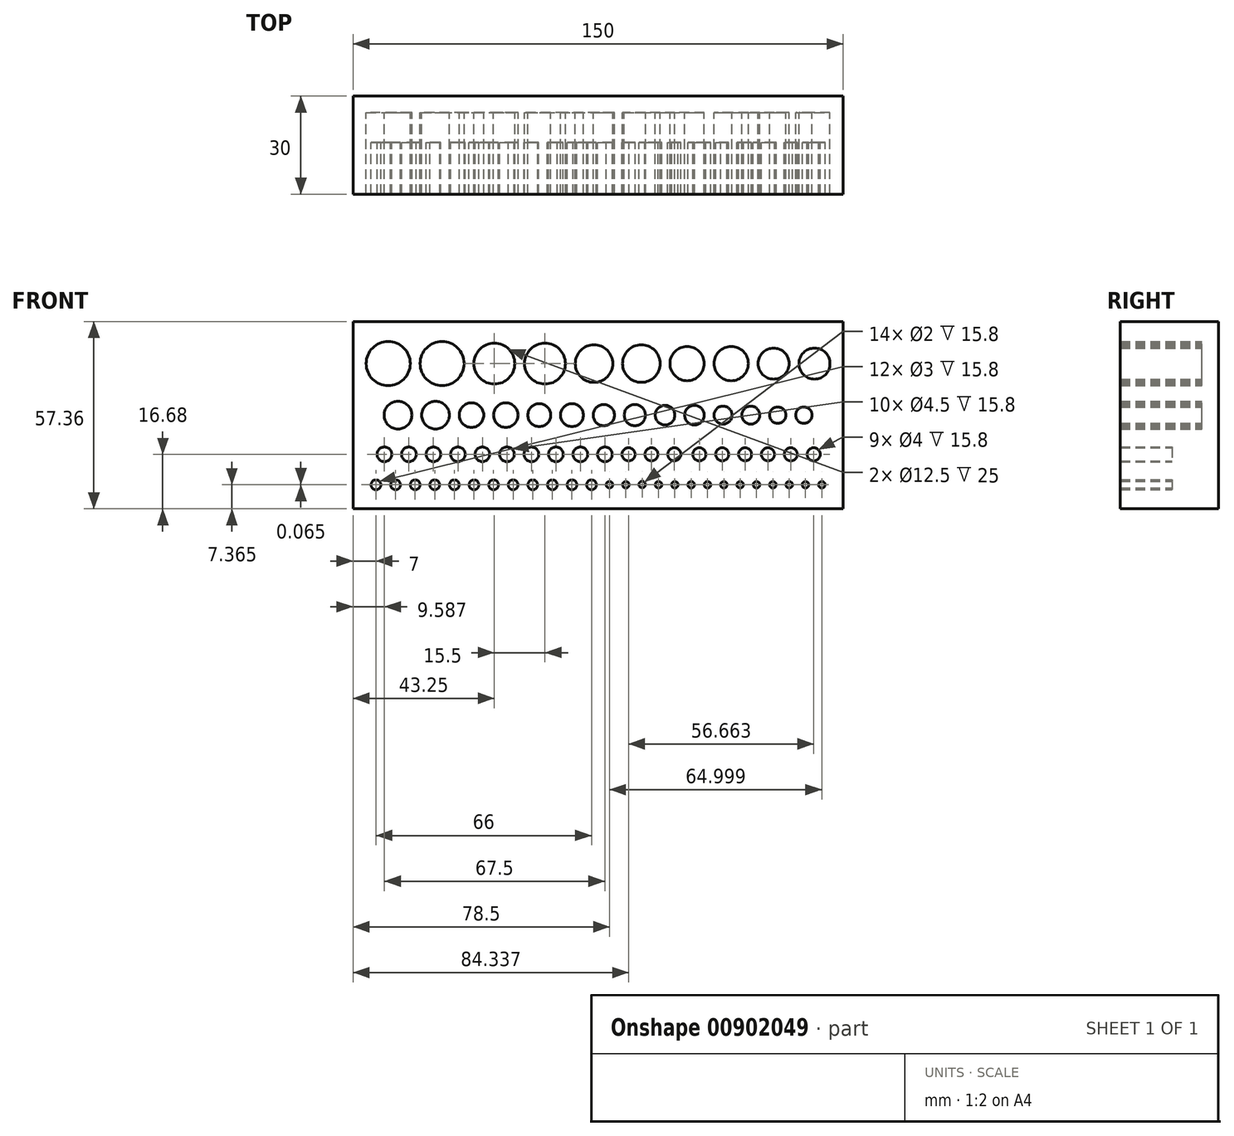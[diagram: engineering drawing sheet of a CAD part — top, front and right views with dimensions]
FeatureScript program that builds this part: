
annotation { "Feature Type Name" : "Feature", "Feature Type Description" : "" }
export const myFeature = defineFeature(function(context is Context, id is Id, definition is map)
    precondition{}
    {
        {
            var Q0;
            Q0=qCreatedBy(makeId("Front.planeOp"),FACE);
            var sketch = newSketch(context, id + "F0", { "sketchPlane" : qUnion([Q0])});
            skLineSegment(sketch, "E0.bottom", {"start": v(75, 28.68) * mm, "end": v(-75, 28.68) * mm});
            skLineSegment(sketch, "E0.top", {"start": v(75, -28.68) * mm, "end": v(-75, -28.68) * mm});
            skLineSegment(sketch, "E0.left", {"start": v(75, 28.68) * mm, "end": v(75, -28.68) * mm});
            skLineSegment(sketch, "E0.right", {"start": v(-75, 28.68) * mm, "end": v(-75, -28.68) * mm});
            skPoint(sketch, "E0.middle", {"position": v(0, 0) * mm});
            skLineSegment(sketch, "E1", {"start": v(-75, 0) * mm, "end": v(75, 0) * mm});
            skLineSegment(sketch, "E2", {"start": v(-75, 15.78) * mm, "end": v(75, 15.78) * mm});
            skLineSegment(sketch, "E3", {"start": v(-75, -12) * mm, "end": v(75, -12) * mm});
            skCircle(sketch, "E4", {"center": v(-64.25, 15.78) * mm, "radius": 6.75 * mm});
            skCircle(sketch, "E5", {"center": v(-47.75, 15.78) * mm, "radius": 6.75 * mm});
            skCircle(sketch, "E6", {"center": v(-31.75, 15.78) * mm, "radius": 6.25 * mm});
            skCircle(sketch, "E7", {"center": v(-16.25, 15.78) * mm, "radius": 6.25 * mm});
            skCircle(sketch, "E8", {"center": v(-1.25, 15.78) * mm, "radius": 5.75 * mm});
            skCircle(sketch, "E9", {"center": v(13.25, 15.78) * mm, "radius": 5.75 * mm});
            skCircle(sketch, "E10", {"center": v(27.25, 15.78) * mm, "radius": 5.25 * mm});
            skCircle(sketch, "E11", {"center": v(40.75, 15.78) * mm, "radius": 5.25 * mm});
            skCircle(sketch, "E12", {"center": v(53.75, 15.78) * mm, "radius": 4.75 * mm});
            skCircle(sketch, "E13", {"center": v(66.25, 15.78) * mm, "radius": 4.75 * mm});
            skCircle(sketch, "E14", {"center": v(-61.25, 0) * mm, "radius": 4.25 * mm});
            skCircle(sketch, "E15", {"center": v(-49.75, 0) * mm, "radius": 4.25 * mm});
            skCircle(sketch, "E16", {"center": v(-38.75, 0) * mm, "radius": 3.75 * mm});
            skCircle(sketch, "E17", {"center": v(-28.25, 0) * mm, "radius": 3.75 * mm});
            skCircle(sketch, "E18", {"center": v(-18, 0) * mm, "radius": 3.5 * mm});
            skCircle(sketch, "E19", {"center": v(-8, 0) * mm, "radius": 3.5 * mm});
            skCircle(sketch, "E20", {"center": v(1.75, 0) * mm, "radius": 3.25 * mm});
            skCircle(sketch, "E21", {"center": v(11.25, 0) * mm, "radius": 3.25 * mm});
            skCircle(sketch, "E22", {"center": v(20.5, 0) * mm, "radius": 3 * mm});
            skCircle(sketch, "E23", {"center": v(29.5, 0) * mm, "radius": 3 * mm});
            skCircle(sketch, "E24", {"center": v(38.25, 0) * mm, "radius": 2.75 * mm});
            skCircle(sketch, "E25", {"center": v(46.75, 0) * mm, "radius": 2.75 * mm});
            skCircle(sketch, "E26", {"center": v(55, 0) * mm, "radius": 2.5 * mm});
            skCircle(sketch, "E27", {"center": v(63, 0) * mm, "radius": 2.5 * mm});
            skCircle(sketch, "E28", {"center": v(-65.41, -12) * mm, "radius": 2.25 * mm});
            skCircle(sketch, "E29", {"center": v(-57.91, -12) * mm, "radius": 2.25 * mm});
            skCircle(sketch, "E30", {"center": v(-50.41, -12) * mm, "radius": 2.25 * mm});
            skCircle(sketch, "E31", {"center": v(-42.91, -12) * mm, "radius": 2.25 * mm});
            skCircle(sketch, "E32", {"center": v(-35.41, -12) * mm, "radius": 2.25 * mm});
            skCircle(sketch, "E33", {"center": v(-27.91, -12) * mm, "radius": 2.25 * mm});
            skCircle(sketch, "E34", {"center": v(-20.41, -12) * mm, "radius": 2.25 * mm});
            skCircle(sketch, "E35", {"center": v(-12.91, -12) * mm, "radius": 2.25 * mm});
            skCircle(sketch, "E36", {"center": v(-5.41, -12) * mm, "radius": 2.25 * mm});
            skCircle(sketch, "E37", {"center": v(2.09, -12) * mm, "radius": 2.25 * mm});
            skCircle(sketch, "E38", {"center": v(9.34, -12) * mm, "radius": 2 * mm});
            skCircle(sketch, "E39", {"center": v(16.34, -12) * mm, "radius": 2 * mm});
            skCircle(sketch, "E40", {"center": v(23.34, -12) * mm, "radius": 2 * mm});
            skCircle(sketch, "E41", {"center": v(31, -12) * mm, "radius": 2 * mm});
            skCircle(sketch, "E42", {"center": v(38, -12) * mm, "radius": 2 * mm});
            skCircle(sketch, "E43", {"center": v(45, -12) * mm, "radius": 2 * mm});
            skCircle(sketch, "E44", {"center": v(52, -12) * mm, "radius": 2 * mm});
            skCircle(sketch, "E45", {"center": v(59, -12) * mm, "radius": 2 * mm});
            skCircle(sketch, "E46", {"center": v(66, -12) * mm, "radius": 2 * mm});
            skLineSegment(sketch, "E47", {"start": v(-75, -21.32) * mm, "end": v(75, -21.32) * mm});
            skCircle(sketch, "E48", {"center": v(-68, -21.32) * mm, "radius": 1.5 * mm});
            skCircle(sketch, "E49", {"center": v(-62, -21.32) * mm, "radius": 1.5 * mm});
            skCircle(sketch, "E50", {"center": v(-56, -21.32) * mm, "radius": 1.5 * mm});
            skCircle(sketch, "E51", {"center": v(-50, -21.32) * mm, "radius": 1.5 * mm});
            skCircle(sketch, "E52", {"center": v(-44, -21.32) * mm, "radius": 1.5 * mm});
            skCircle(sketch, "E53", {"center": v(-38, -21.32) * mm, "radius": 1.5 * mm});
            skCircle(sketch, "E54", {"center": v(-32, -21.32) * mm, "radius": 1.5 * mm});
            skCircle(sketch, "E55", {"center": v(-26, -21.32) * mm, "radius": 1.5 * mm});
            skCircle(sketch, "E56", {"center": v(-20, -21.32) * mm, "radius": 1.5 * mm});
            skCircle(sketch, "E57", {"center": v(-14, -21.32) * mm, "radius": 1.5 * mm});
            skCircle(sketch, "E58", {"center": v(-8, -21.32) * mm, "radius": 1.5 * mm});
            skCircle(sketch, "E59", {"center": v(-2, -21.32) * mm, "radius": 1.5 * mm});
            skCircle(sketch, "E60", {"center": v(3.5, -21.32) * mm, "radius": 1 * mm});
            skCircle(sketch, "E61", {"center": v(8.5, -21.32) * mm, "radius": 1 * mm});
            skCircle(sketch, "E62", {"center": v(13.5, -21.25) * mm, "radius": 1 * mm});
            skCircle(sketch, "E63", {"center": v(18.5, -21.32) * mm, "radius": 1 * mm});
            skCircle(sketch, "E64", {"center": v(23.5, -21.32) * mm, "radius": 1 * mm});
            skCircle(sketch, "E65", {"center": v(28.5, -21.32) * mm, "radius": 1 * mm});
            skCircle(sketch, "E66", {"center": v(33.5, -21.32) * mm, "radius": 1 * mm});
            skCircle(sketch, "E67", {"center": v(38.5, -21.32) * mm, "radius": 1 * mm});
            skCircle(sketch, "E68", {"center": v(43.5, -21.32) * mm, "radius": 1 * mm});
            skCircle(sketch, "E69", {"center": v(48.5, -21.32) * mm, "radius": 1 * mm});
            skCircle(sketch, "E70", {"center": v(53.5, -21.32) * mm, "radius": 1 * mm});
            skCircle(sketch, "E71", {"center": v(58.5, -21.32) * mm, "radius": 1 * mm});
            skCircle(sketch, "E72", {"center": v(63.5, -21.32) * mm, "radius": 1 * mm});
            skCircle(sketch, "E73", {"center": v(68.5, -21.32) * mm, "radius": 1 * mm});
            skSolve(sketch);
        }
        {
            var Q0;
            Q0=qSketchRegion(id+"F0",true);
            extrude(context, id + "F1", {"entities" : qUnion([Q0]), "depth" : 25 * mm, "offsetDistance" : 25 * mm});
        }
        {
            var Q0;
            Q0=makeQuery(id+"F1.opExtrude","CAP_FACE",FACE,{"disambiguationData":[OSD([sQuery(id+"F0.wireOp",EDGE,"E0.bottom"),sQuery(id+"F0.wireOp",EDGE,"E0.top"),sQuery(id+"F0.wireOp",EDGE,"E0.left"),sQuery(id+"F0.wireOp",EDGE,"E0.right"),sQuery(id+"F0.wireOp",EDGE,"E4"),sQuery(id+"F0.wireOp",EDGE,"E5"),sQuery(id+"F0.wireOp",EDGE,"E6"),sQuery(id+"F0.wireOp",EDGE,"E7"),sQuery(id+"F0.wireOp",EDGE,"E8"),sQuery(id+"F0.wireOp",EDGE,"E9"),sQuery(id+"F0.wireOp",EDGE,"E10"),sQuery(id+"F0.wireOp",EDGE,"E11"),sQuery(id+"F0.wireOp",EDGE,"E12"),sQuery(id+"F0.wireOp",EDGE,"E13"),sQuery(id+"F0.wireOp",EDGE,"E14"),sQuery(id+"F0.wireOp",EDGE,"E15"),sQuery(id+"F0.wireOp",EDGE,"E16"),sQuery(id+"F0.wireOp",EDGE,"E17"),sQuery(id+"F0.wireOp",EDGE,"E18"),sQuery(id+"F0.wireOp",EDGE,"E19"),sQuery(id+"F0.wireOp",EDGE,"E20"),sQuery(id+"F0.wireOp",EDGE,"E21"),sQuery(id+"F0.wireOp",EDGE,"E22"),sQuery(id+"F0.wireOp",EDGE,"E23"),sQuery(id+"F0.wireOp",EDGE,"E24"),sQuery(id+"F0.wireOp",EDGE,"E25"),sQuery(id+"F0.wireOp",EDGE,"E26"),sQuery(id+"F0.wireOp",EDGE,"E27"),sQuery(id+"F0.wireOp",EDGE,"E28"),sQuery(id+"F0.wireOp",EDGE,"E29"),sQuery(id+"F0.wireOp",EDGE,"E30"),sQuery(id+"F0.wireOp",EDGE,"E31"),sQuery(id+"F0.wireOp",EDGE,"E32"),sQuery(id+"F0.wireOp",EDGE,"E33"),sQuery(id+"F0.wireOp",EDGE,"E34"),sQuery(id+"F0.wireOp",EDGE,"E35"),sQuery(id+"F0.wireOp",EDGE,"E36"),sQuery(id+"F0.wireOp",EDGE,"E37"),sQuery(id+"F0.wireOp",EDGE,"E38"),sQuery(id+"F0.wireOp",EDGE,"E39"),sQuery(id+"F0.wireOp",EDGE,"E40"),sQuery(id+"F0.wireOp",EDGE,"E41"),sQuery(id+"F0.wireOp",EDGE,"E42"),sQuery(id+"F0.wireOp",EDGE,"E43"),sQuery(id+"F0.wireOp",EDGE,"E44"),sQuery(id+"F0.wireOp",EDGE,"E45"),sQuery(id+"F0.wireOp",EDGE,"E46"),sQuery(id+"F0.wireOp",EDGE,"E48"),sQuery(id+"F0.wireOp",EDGE,"E49"),sQuery(id+"F0.wireOp",EDGE,"E50"),sQuery(id+"F0.wireOp",EDGE,"E51"),sQuery(id+"F0.wireOp",EDGE,"E52"),sQuery(id+"F0.wireOp",EDGE,"E53"),sQuery(id+"F0.wireOp",EDGE,"E54"),sQuery(id+"F0.wireOp",EDGE,"E55"),sQuery(id+"F0.wireOp",EDGE,"E56"),sQuery(id+"F0.wireOp",EDGE,"E57"),sQuery(id+"F0.wireOp",EDGE,"E58"),sQuery(id+"F0.wireOp",EDGE,"E59"),sQuery(id+"F0.wireOp",EDGE,"E60"),sQuery(id+"F0.wireOp",EDGE,"E61"),sQuery(id+"F0.wireOp",EDGE,"E62"),sQuery(id+"F0.wireOp",EDGE,"E63"),sQuery(id+"F0.wireOp",EDGE,"E64"),sQuery(id+"F0.wireOp",EDGE,"E65"),sQuery(id+"F0.wireOp",EDGE,"E66"),sQuery(id+"F0.wireOp",EDGE,"E67"),sQuery(id+"F0.wireOp",EDGE,"E68"),sQuery(id+"F0.wireOp",EDGE,"E69"),sQuery(id+"F0.wireOp",EDGE,"E70"),sQuery(id+"F0.wireOp",EDGE,"E71"),sQuery(id+"F0.wireOp",EDGE,"E72"),sQuery(id+"F0.wireOp",EDGE,"E73")])],"isStart":true});
            var sketch = newSketch(context, id + "F2", { "sketchPlane" : qUnion([Q0])});
            skLineSegment(sketch, "E74.bottom", {"start": v(-72.47, -7.03) * mm, "end": v(72.05, -7.03) * mm});
            skLineSegment(sketch, "E74.top", {"start": v(-72.47, -24.86) * mm, "end": v(72.05, -24.86) * mm});
            skLineSegment(sketch, "E74.left", {"start": v(-72.47, -7.03) * mm, "end": v(-72.47, -24.86) * mm});
            skLineSegment(sketch, "E74.right", {"start": v(72.05, -7.03) * mm, "end": v(72.05, -24.86) * mm});
            skSolve(sketch);
        }
        {
            var Q0;
            Q0=qSketchRegion(id+"F2",true);
            extrude(context, id + "F3", {"entities" : qUnion([Q0]), "operationType" : NewBodyOperationType.ADD, "oppositeDirection" : true, "depth" : 9.2 * mm, "offsetDistance" : 25 * mm});
        }
        {
            var Q0;
            Q0=makeQuery(id+"F3.boolean.opBoolean","MERGE",FACE,{"derivedFrom":[makeQuery(id+"F1.opExtrude","CAP_FACE",FACE,{"disambiguationData":[OSD([sQuery(id+"F0.wireOp",EDGE,"E0.bottom"),sQuery(id+"F0.wireOp",EDGE,"E0.top"),sQuery(id+"F0.wireOp",EDGE,"E0.left"),sQuery(id+"F0.wireOp",EDGE,"E0.right"),sQuery(id+"F0.wireOp",EDGE,"E4"),sQuery(id+"F0.wireOp",EDGE,"E5"),sQuery(id+"F0.wireOp",EDGE,"E6"),sQuery(id+"F0.wireOp",EDGE,"E7"),sQuery(id+"F0.wireOp",EDGE,"E8"),sQuery(id+"F0.wireOp",EDGE,"E9"),sQuery(id+"F0.wireOp",EDGE,"E10"),sQuery(id+"F0.wireOp",EDGE,"E11"),sQuery(id+"F0.wireOp",EDGE,"E12"),sQuery(id+"F0.wireOp",EDGE,"E13"),sQuery(id+"F0.wireOp",EDGE,"E14"),sQuery(id+"F0.wireOp",EDGE,"E15"),sQuery(id+"F0.wireOp",EDGE,"E16"),sQuery(id+"F0.wireOp",EDGE,"E17"),sQuery(id+"F0.wireOp",EDGE,"E18"),sQuery(id+"F0.wireOp",EDGE,"E19"),sQuery(id+"F0.wireOp",EDGE,"E20"),sQuery(id+"F0.wireOp",EDGE,"E21"),sQuery(id+"F0.wireOp",EDGE,"E22"),sQuery(id+"F0.wireOp",EDGE,"E23"),sQuery(id+"F0.wireOp",EDGE,"E24"),sQuery(id+"F0.wireOp",EDGE,"E25"),sQuery(id+"F0.wireOp",EDGE,"E26"),sQuery(id+"F0.wireOp",EDGE,"E27"),sQuery(id+"F0.wireOp",EDGE,"E28"),sQuery(id+"F0.wireOp",EDGE,"E29"),sQuery(id+"F0.wireOp",EDGE,"E30"),sQuery(id+"F0.wireOp",EDGE,"E31"),sQuery(id+"F0.wireOp",EDGE,"E32"),sQuery(id+"F0.wireOp",EDGE,"E33"),sQuery(id+"F0.wireOp",EDGE,"E34"),sQuery(id+"F0.wireOp",EDGE,"E35"),sQuery(id+"F0.wireOp",EDGE,"E36"),sQuery(id+"F0.wireOp",EDGE,"E37"),sQuery(id+"F0.wireOp",EDGE,"E38"),sQuery(id+"F0.wireOp",EDGE,"E39"),sQuery(id+"F0.wireOp",EDGE,"E40"),sQuery(id+"F0.wireOp",EDGE,"E41"),sQuery(id+"F0.wireOp",EDGE,"E42"),sQuery(id+"F0.wireOp",EDGE,"E43"),sQuery(id+"F0.wireOp",EDGE,"E44"),sQuery(id+"F0.wireOp",EDGE,"E45"),sQuery(id+"F0.wireOp",EDGE,"E46"),sQuery(id+"F0.wireOp",EDGE,"E48"),sQuery(id+"F0.wireOp",EDGE,"E49"),sQuery(id+"F0.wireOp",EDGE,"E50"),sQuery(id+"F0.wireOp",EDGE,"E51"),sQuery(id+"F0.wireOp",EDGE,"E52"),sQuery(id+"F0.wireOp",EDGE,"E53"),sQuery(id+"F0.wireOp",EDGE,"E54"),sQuery(id+"F0.wireOp",EDGE,"E55"),sQuery(id+"F0.wireOp",EDGE,"E56"),sQuery(id+"F0.wireOp",EDGE,"E57"),sQuery(id+"F0.wireOp",EDGE,"E58"),sQuery(id+"F0.wireOp",EDGE,"E59"),sQuery(id+"F0.wireOp",EDGE,"E60"),sQuery(id+"F0.wireOp",EDGE,"E61"),sQuery(id+"F0.wireOp",EDGE,"E62"),sQuery(id+"F0.wireOp",EDGE,"E63"),sQuery(id+"F0.wireOp",EDGE,"E64"),sQuery(id+"F0.wireOp",EDGE,"E65"),sQuery(id+"F0.wireOp",EDGE,"E66"),sQuery(id+"F0.wireOp",EDGE,"E67"),sQuery(id+"F0.wireOp",EDGE,"E68"),sQuery(id+"F0.wireOp",EDGE,"E69"),sQuery(id+"F0.wireOp",EDGE,"E70"),sQuery(id+"F0.wireOp",EDGE,"E71"),sQuery(id+"F0.wireOp",EDGE,"E72"),sQuery(id+"F0.wireOp",EDGE,"E73")])],"isStart":true}),makeQuery(id+"F3.opExtrude","CAP_FACE",FACE,{"disambiguationData":[OSD([sQuery(id+"F2.wireOp",EDGE,"E74.bottom"),sQuery(id+"F2.wireOp",EDGE,"E74.top"),sQuery(id+"F2.wireOp",EDGE,"E74.left"),sQuery(id+"F2.wireOp",EDGE,"E74.right")])],"isStart":true})]});
            var sketch = newSketch(context, id + "F4", { "sketchPlane" : qUnion([Q0])});
            skLineSegment(sketch, "E75.bottom", {"start": v(-75, 28.68) * mm, "end": v(75, 28.68) * mm});
            skLineSegment(sketch, "E75.top", {"start": v(-75, -28.68) * mm, "end": v(75, -28.68) * mm});
            skLineSegment(sketch, "E75.left", {"start": v(-75, 28.68) * mm, "end": v(-75, -28.68) * mm});
            skLineSegment(sketch, "E75.right", {"start": v(75, 28.68) * mm, "end": v(75, -28.68) * mm});
            skSolve(sketch);
        }
        {
            var Q0;
            Q0=qSketchRegion(id+"F4",true);
            extrude(context, id + "F5", {"entities" : qUnion([Q0]), "operationType" : NewBodyOperationType.ADD, "depth" : 5 * mm, "offsetDistance" : 25 * mm});
        }
    });
